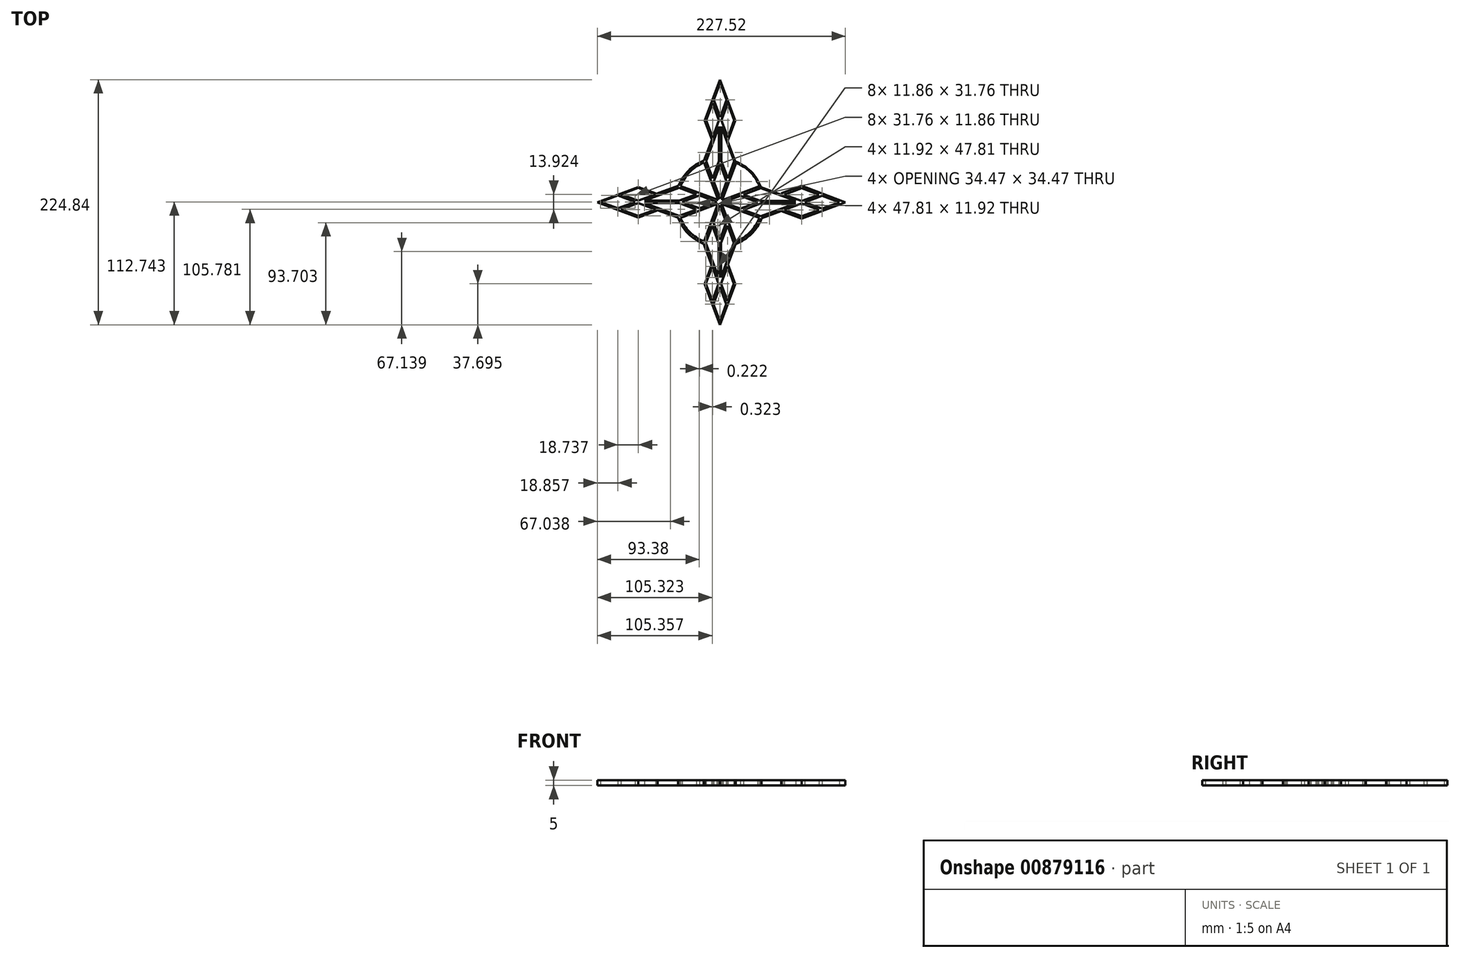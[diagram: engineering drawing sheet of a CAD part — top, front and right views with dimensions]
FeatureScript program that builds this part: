
annotation { "Feature Type Name" : "Feature", "Feature Type Description" : "" }
export const myFeature = defineFeature(function(context is Context, id is Id, definition is map)
    precondition{}
    {
        {
            var Q0;
            Q0=qCreatedBy(makeId("Top.planeOp"),FACE);
            var sketch = newSketch(context, id + "F0", { "sketchPlane" : qUnion([Q0])});
            skLineSegment(sketch, "E0", {"start": v(0, 0) * mm, "end": v(-14, 37.47) * mm});
            skLineSegment(sketch, "E1", {"start": v(-14, 37.47) * mm, "end": v(0, 74.95) * mm});
            skLineSegment(sketch, "E2", {"start": v(0, 74.95) * mm, "end": v(14, 37.47) * mm});
            skLineSegment(sketch, "E3", {"start": v(14, 37.47) * mm, "end": v(0, 0) * mm});
            skLineSegment(sketch, "E4", {"start": v(0, 74.95) * mm, "end": v(0, 37.47) * mm});
            skLineSegment(sketch, "E5", {"start": v(0, 37.47) * mm, "end": v(-7, 18.74) * mm});
            skLineSegment(sketch, "E6", {"start": v(0, 37.47) * mm, "end": v(7, 18.74) * mm});
            skLineSegment(sketch, "E7", {"start": v(-7, 56.2) * mm, "end": v(-14, 74.95) * mm});
            skLineSegment(sketch, "E8", {"start": v(-14, 74.95) * mm, "end": v(0, 112.42) * mm});
            skLineSegment(sketch, "E9", {"start": v(0, 112.42) * mm, "end": v(14, 74.95) * mm});
            skLineSegment(sketch, "E10", {"start": v(14, 74.95) * mm, "end": v(7, 56.2) * mm});
            skLineSegment(sketch, "E11", {"start": v(-7, 93.68) * mm, "end": v(0, 74.95) * mm});
            skLineSegment(sketch, "E12", {"start": v(7, 93.68) * mm, "end": v(0, 74.95) * mm});
            skLineSegment(sketch, "E13.1.0", {"start": v(-37.47, -14) * mm, "end": v(-74.95, 0) * mm});
            skLineSegment(sketch, "E13.1.1", {"start": v(-74.95, 0) * mm, "end": v(-37.47, 14) * mm});
            skLineSegment(sketch, "E13.1.2", {"start": v(-37.47, 0) * mm, "end": v(-18.74, 7) * mm});
            skLineSegment(sketch, "E13.1.3", {"start": v(-74.95, 0) * mm, "end": v(-37.47, 0) * mm});
            skLineSegment(sketch, "E13.1.4", {"start": v(-93.68, 7) * mm, "end": v(-74.95, 0) * mm});
            skLineSegment(sketch, "E13.1.5", {"start": v(-56.2, -7) * mm, "end": v(-74.95, -14) * mm});
            skLineSegment(sketch, "E13.1.6", {"start": v(-74.95, -14) * mm, "end": v(-112.42, 0) * mm});
            skLineSegment(sketch, "E13.1.7", {"start": v(-112.42, 0) * mm, "end": v(-74.95, 14) * mm});
            skLineSegment(sketch, "E13.1.8", {"start": v(-37.47, 0) * mm, "end": v(-18.74, -7) * mm});
            skLineSegment(sketch, "E13.1.9", {"start": v(-93.68, -7) * mm, "end": v(-74.95, 0) * mm});
            skLineSegment(sketch, "E13.1.10", {"start": v(-74.95, 14) * mm, "end": v(-56.2, 7) * mm});
            skLineSegment(sketch, "E13.1.11", {"start": v(0, 0) * mm, "end": v(-37.47, -14) * mm});
            skLineSegment(sketch, "E13.1.12", {"start": v(-37.47, 14) * mm, "end": v(0, 0) * mm});
            skLineSegment(sketch, "E13.2.0", {"start": v(14, -37.47) * mm, "end": v(0, -74.95) * mm});
            skLineSegment(sketch, "E13.2.1", {"start": v(0, -74.95) * mm, "end": v(-14, -37.47) * mm});
            skLineSegment(sketch, "E13.2.2", {"start": v(0, -37.47) * mm, "end": v(-7, -18.74) * mm});
            skLineSegment(sketch, "E13.2.3", {"start": v(0, -74.95) * mm, "end": v(0, -37.47) * mm});
            skLineSegment(sketch, "E13.2.4", {"start": v(-7, -93.68) * mm, "end": v(0, -74.95) * mm});
            skLineSegment(sketch, "E13.2.5", {"start": v(7, -56.2) * mm, "end": v(14, -74.95) * mm});
            skLineSegment(sketch, "E13.2.6", {"start": v(14, -74.95) * mm, "end": v(0, -112.42) * mm});
            skLineSegment(sketch, "E13.2.7", {"start": v(0, -112.42) * mm, "end": v(-14, -74.95) * mm});
            skLineSegment(sketch, "E13.2.8", {"start": v(0, -37.47) * mm, "end": v(7, -18.74) * mm});
            skLineSegment(sketch, "E13.2.9", {"start": v(7, -93.68) * mm, "end": v(0, -74.95) * mm});
            skLineSegment(sketch, "E13.2.10", {"start": v(-14, -74.95) * mm, "end": v(-7, -56.2) * mm});
            skLineSegment(sketch, "E13.2.11", {"start": v(0, 0) * mm, "end": v(14, -37.47) * mm});
            skLineSegment(sketch, "E13.2.12", {"start": v(-14, -37.47) * mm, "end": v(0, 0) * mm});
            skLineSegment(sketch, "E13.3.0", {"start": v(37.47, 14) * mm, "end": v(74.95, 0) * mm});
            skLineSegment(sketch, "E13.3.1", {"start": v(74.95, 0) * mm, "end": v(37.47, -14) * mm});
            skLineSegment(sketch, "E13.3.2", {"start": v(37.47, 0) * mm, "end": v(18.74, -7) * mm});
            skLineSegment(sketch, "E13.3.3", {"start": v(74.95, 0) * mm, "end": v(37.47, 0) * mm});
            skLineSegment(sketch, "E13.3.4", {"start": v(93.68, -7) * mm, "end": v(74.95, 0) * mm});
            skLineSegment(sketch, "E13.3.5", {"start": v(56.2, 7) * mm, "end": v(74.95, 14) * mm});
            skLineSegment(sketch, "E13.3.6", {"start": v(74.95, 14) * mm, "end": v(112.42, 0) * mm});
            skLineSegment(sketch, "E13.3.7", {"start": v(112.42, 0) * mm, "end": v(74.95, -14) * mm});
            skLineSegment(sketch, "E13.3.8", {"start": v(37.47, 0) * mm, "end": v(18.74, 7) * mm});
            skLineSegment(sketch, "E13.3.9", {"start": v(93.68, 7) * mm, "end": v(74.95, 0) * mm});
            skLineSegment(sketch, "E13.3.10", {"start": v(74.95, -14) * mm, "end": v(56.2, -7) * mm});
            skLineSegment(sketch, "E13.3.11", {"start": v(0, 0) * mm, "end": v(37.47, 14) * mm});
            skLineSegment(sketch, "E13.3.12", {"start": v(37.47, -14) * mm, "end": v(0, 0) * mm});
            skPoint(sketch, "E13.center", {"position": v(0, 0) * mm});
            skArc(sketch, "E14", {"start": v(14, 37.47) * mm, "mid": v(28.28, 28.28) * mm, "end": v(37.47, 14) * mm});
            skArc(sketch, "E15.1.0", {"start": v(-37.47, 14) * mm, "mid": v(-28.28, 28.28) * mm, "end": v(-14, 37.47) * mm});
            skArc(sketch, "E15.2.0", {"start": v(-14, -37.47) * mm, "mid": v(-28.28, -28.28) * mm, "end": v(-37.47, -14) * mm});
            skArc(sketch, "E16.3.3.0", {"start": v(37.47, -14) * mm, "mid": v(28.28, -28.28) * mm, "end": v(14, -37.47) * mm});
            skLineSegment(sketch, "E17", {"start": v(0, 0) * mm, "end": v(18.74, 7) * mm});
            skLineSegment(sketch, "E18", {"start": v(2.86, 0) * mm, "end": v(18.74, 5.93) * mm});
            skLineSegment(sketch, "E19", {"start": v(18.74, 5.93) * mm, "end": v(34.61, 0) * mm});
            skLineSegment(sketch, "E20", {"start": v(34.61, 0) * mm, "end": v(18.74, -5.93) * mm});
            skLineSegment(sketch, "E21", {"start": v(18.74, -5.93) * mm, "end": v(2.86, 0) * mm});
            skLineSegment(sketch, "E22", {"start": v(21.6, 7) * mm, "end": v(37.47, 12.92) * mm});
            skLineSegment(sketch, "E23", {"start": v(37.47, 12.92) * mm, "end": v(69.4, 1) * mm});
            skLineSegment(sketch, "E24", {"start": v(69.4, 1) * mm, "end": v(37.47, 1) * mm});
            skLineSegment(sketch, "E25", {"start": v(37.47, 1) * mm, "end": v(21.6, 7) * mm});
            skLineSegment(sketch, "E26", {"start": v(59.07, 7) * mm, "end": v(74.95, 12.92) * mm});
            skLineSegment(sketch, "E27", {"start": v(74.95, 12.92) * mm, "end": v(90.82, 7) * mm});
            skLineSegment(sketch, "E28", {"start": v(90.82, 7) * mm, "end": v(74.95, 1.07) * mm});
            skLineSegment(sketch, "E29", {"start": v(74.95, 1.07) * mm, "end": v(59.07, 7) * mm});
            skLineSegment(sketch, "E30", {"start": v(77.8, 0) * mm, "end": v(93.68, 5.93) * mm});
            skLineSegment(sketch, "E31", {"start": v(93.68, 5.93) * mm, "end": v(109.56, 0) * mm});
            skLineSegment(sketch, "E32", {"start": v(109.56, 0) * mm, "end": v(93.68, -5.93) * mm});
            skLineSegment(sketch, "E33", {"start": v(93.68, -5.93) * mm, "end": v(77.8, 0) * mm});
            skLineSegment(sketch, "E34", {"start": v(59.07, -7) * mm, "end": v(74.95, -1.07) * mm});
            skLineSegment(sketch, "E35", {"start": v(74.95, -1.07) * mm, "end": v(90.82, -7) * mm});
            skLineSegment(sketch, "E36", {"start": v(90.82, -7) * mm, "end": v(74.95, -12.92) * mm});
            skLineSegment(sketch, "E37", {"start": v(74.95, -12.92) * mm, "end": v(59.07, -7) * mm});
            skLineSegment(sketch, "E38.0", {"start": v(1.7, -1.7) * mm, "end": v(14.57, -36.17) * mm});
            skLineSegment(sketch, "E38.1", {"start": v(36.17, -14.57) * mm, "end": v(1.7, -1.7) * mm});
            skArc(sketch, "E38.2", {"start": v(36.17, -14.57) * mm, "mid": v(27.58, -27.58) * mm, "end": v(14.57, -36.17) * mm});
            skLineSegment(sketch, "E39.MirrorCS", {"start": v(69.4, -1) * mm, "end": v(37.47, -1) * mm});
            skLineSegment(sketch, "E40.MirrorCS", {"start": v(37.47, -1) * mm, "end": v(21.6, -7) * mm});
            skLineSegment(sketch, "E41.MirrorCS", {"start": v(21.6, -7) * mm, "end": v(37.47, -12.92) * mm});
            skLineSegment(sketch, "E42.MirrorCS", {"start": v(37.47, -12.92) * mm, "end": v(69.4, -1) * mm});
            skLineSegment(sketch, "E43.1.0", {"start": v(-6.77, 21.7) * mm, "end": v(-12.7, 37.57) * mm});
            skLineSegment(sketch, "E43.1.1", {"start": v(-12.7, 37.57) * mm, "end": v(-0.78, 69.51) * mm});
            skLineSegment(sketch, "E43.1.2", {"start": v(-0.78, 37.57) * mm, "end": v(-6.77, 21.7) * mm});
            skLineSegment(sketch, "E43.1.3", {"start": v(-0.78, 69.51) * mm, "end": v(-0.78, 37.57) * mm});
            skLineSegment(sketch, "E43.1.4", {"start": v(-5.7, 18.84) * mm, "end": v(0.22, 34.72) * mm});
            skLineSegment(sketch, "E43.1.5", {"start": v(0.22, 2.96) * mm, "end": v(-5.7, 18.84) * mm});
            skLineSegment(sketch, "E43.1.6", {"start": v(6.15, 18.84) * mm, "end": v(0.22, 2.96) * mm});
            skLineSegment(sketch, "E43.1.7", {"start": v(0.22, 34.72) * mm, "end": v(6.15, 18.84) * mm});
            skLineSegment(sketch, "E43.1.8", {"start": v(14.8, 36.28) * mm, "end": v(1.93, 1.8) * mm});
            skLineSegment(sketch, "E43.1.9", {"start": v(1.93, 1.8) * mm, "end": v(36.4, 14.67) * mm});
            skArc(sketch, "E43.1.10", {"start": v(14.8, 36.28) * mm, "mid": v(27.8, 27.68) * mm, "end": v(36.4, 14.67) * mm});
            skLineSegment(sketch, "E43.1.11", {"start": v(1.22, 37.57) * mm, "end": v(7.22, 21.7) * mm});
            skLineSegment(sketch, "E43.1.12", {"start": v(7.22, 21.7) * mm, "end": v(13.15, 37.57) * mm});
            skLineSegment(sketch, "E43.1.13", {"start": v(1.22, 69.51) * mm, "end": v(1.22, 37.57) * mm});
            skLineSegment(sketch, "E43.1.14", {"start": v(13.15, 37.57) * mm, "end": v(1.22, 69.51) * mm});
            skLineSegment(sketch, "E43.1.15", {"start": v(13.15, 75.05) * mm, "end": v(7.22, 59.17) * mm});
            skLineSegment(sketch, "E43.1.16", {"start": v(7.22, 59.17) * mm, "end": v(1.29, 75.05) * mm});
            skLineSegment(sketch, "E43.1.17", {"start": v(1.29, 75.05) * mm, "end": v(7.22, 90.93) * mm});
            skLineSegment(sketch, "E43.1.18", {"start": v(7.22, 90.93) * mm, "end": v(13.15, 75.05) * mm});
            skLineSegment(sketch, "E43.1.19", {"start": v(6.15, 93.78) * mm, "end": v(0.22, 77.9) * mm});
            skLineSegment(sketch, "E43.1.20", {"start": v(0.22, 77.9) * mm, "end": v(-5.7, 93.78) * mm});
            skLineSegment(sketch, "E43.1.21", {"start": v(-5.7, 93.78) * mm, "end": v(0.22, 109.66) * mm});
            skLineSegment(sketch, "E43.1.22", {"start": v(0.22, 109.66) * mm, "end": v(6.15, 93.78) * mm});
            skLineSegment(sketch, "E43.1.23", {"start": v(-6.77, 90.93) * mm, "end": v(-0.85, 75.05) * mm});
            skLineSegment(sketch, "E43.1.24", {"start": v(-12.7, 75.05) * mm, "end": v(-6.77, 90.93) * mm});
            skLineSegment(sketch, "E43.1.25", {"start": v(-6.77, 59.17) * mm, "end": v(-12.7, 75.05) * mm});
            skLineSegment(sketch, "E43.1.26", {"start": v(-0.85, 75.05) * mm, "end": v(-6.77, 59.17) * mm});
            skLineSegment(sketch, "E43.2.0", {"start": v(-21.48, -6.67) * mm, "end": v(-37.35, -12.6) * mm});
            skLineSegment(sketch, "E43.2.1", {"start": v(-37.35, -12.6) * mm, "end": v(-69.29, -0.68) * mm});
            skLineSegment(sketch, "E43.2.2", {"start": v(-37.35, -0.68) * mm, "end": v(-21.48, -6.67) * mm});
            skLineSegment(sketch, "E43.2.3", {"start": v(-69.29, -0.68) * mm, "end": v(-37.35, -0.68) * mm});
            skLineSegment(sketch, "E43.2.4", {"start": v(-18.62, -5.6) * mm, "end": v(-34.5, 0.32) * mm});
            skLineSegment(sketch, "E43.2.5", {"start": v(-2.74, 0.32) * mm, "end": v(-18.62, -5.6) * mm});
            skLineSegment(sketch, "E43.2.6", {"start": v(-18.62, 6.25) * mm, "end": v(-2.74, 0.32) * mm});
            skLineSegment(sketch, "E43.2.7", {"start": v(-34.5, 0.32) * mm, "end": v(-18.62, 6.25) * mm});
            skLineSegment(sketch, "E43.2.8", {"start": v(-36.05, 14.9) * mm, "end": v(-1.58, 2.03) * mm});
            skLineSegment(sketch, "E43.2.9", {"start": v(-1.58, 2.03) * mm, "end": v(-14.45, 36.5) * mm});
            skArc(sketch, "E43.2.10", {"start": v(-36.05, 14.9) * mm, "mid": v(-27.46, 27.9) * mm, "end": v(-14.45, 36.5) * mm});
            skLineSegment(sketch, "E43.2.11", {"start": v(-37.35, 1.32) * mm, "end": v(-21.48, 7.32) * mm});
            skLineSegment(sketch, "E43.2.12", {"start": v(-21.48, 7.32) * mm, "end": v(-37.35, 13.25) * mm});
            skLineSegment(sketch, "E43.2.13", {"start": v(-69.29, 1.32) * mm, "end": v(-37.35, 1.32) * mm});
            skLineSegment(sketch, "E43.2.14", {"start": v(-37.35, 13.25) * mm, "end": v(-69.29, 1.32) * mm});
            skLineSegment(sketch, "E43.2.15", {"start": v(-74.83, 13.25) * mm, "end": v(-58.95, 7.32) * mm});
            skLineSegment(sketch, "E43.2.16", {"start": v(-58.95, 7.32) * mm, "end": v(-74.83, 1.4) * mm});
            skLineSegment(sketch, "E43.2.17", {"start": v(-74.83, 1.4) * mm, "end": v(-90.7, 7.32) * mm});
            skLineSegment(sketch, "E43.2.18", {"start": v(-90.7, 7.32) * mm, "end": v(-74.83, 13.25) * mm});
            skLineSegment(sketch, "E43.2.19", {"start": v(-93.56, 6.25) * mm, "end": v(-77.68, 0.32) * mm});
            skLineSegment(sketch, "E43.2.20", {"start": v(-77.68, 0.32) * mm, "end": v(-93.56, -5.6) * mm});
            skLineSegment(sketch, "E43.2.21", {"start": v(-93.56, -5.6) * mm, "end": v(-109.44, 0.32) * mm});
            skLineSegment(sketch, "E43.2.22", {"start": v(-109.44, 0.32) * mm, "end": v(-93.56, 6.25) * mm});
            skLineSegment(sketch, "E43.2.23", {"start": v(-90.7, -6.67) * mm, "end": v(-74.83, -0.74) * mm});
            skLineSegment(sketch, "E43.2.24", {"start": v(-74.83, -12.6) * mm, "end": v(-90.7, -6.67) * mm});
            skLineSegment(sketch, "E43.2.25", {"start": v(-58.95, -6.67) * mm, "end": v(-74.83, -12.6) * mm});
            skLineSegment(sketch, "E43.2.26", {"start": v(-74.83, -0.74) * mm, "end": v(-58.95, -6.67) * mm});
            skLineSegment(sketch, "E43.3.0", {"start": v(6.9, -21.37) * mm, "end": v(12.82, -37.25) * mm});
            skLineSegment(sketch, "E43.3.1", {"start": v(12.82, -37.25) * mm, "end": v(0.9, -69.19) * mm});
            skLineSegment(sketch, "E43.3.2", {"start": v(0.9, -37.25) * mm, "end": v(6.9, -21.37) * mm});
            skLineSegment(sketch, "E43.3.3", {"start": v(0.9, -69.19) * mm, "end": v(0.9, -37.25) * mm});
            skLineSegment(sketch, "E43.3.4", {"start": v(5.83, -18.51) * mm, "end": v(-0.1, -34.4) * mm});
            skLineSegment(sketch, "E43.3.5", {"start": v(-0.1, -2.64) * mm, "end": v(5.83, -18.51) * mm});
            skLineSegment(sketch, "E43.3.6", {"start": v(-6.03, -18.51) * mm, "end": v(-0.1, -2.64) * mm});
            skLineSegment(sketch, "E43.3.7", {"start": v(-0.1, -34.4) * mm, "end": v(-6.03, -18.51) * mm});
            skLineSegment(sketch, "E43.3.8", {"start": v(-14.67, -35.95) * mm, "end": v(-1.8, -1.48) * mm});
            skLineSegment(sketch, "E43.3.9", {"start": v(-1.8, -1.48) * mm, "end": v(-36.28, -14.35) * mm});
            skArc(sketch, "E43.3.10", {"start": v(-14.67, -35.95) * mm, "mid": v(-27.68, -27.36) * mm, "end": v(-36.28, -14.35) * mm});
            skLineSegment(sketch, "E43.3.11", {"start": v(-1.1, -37.25) * mm, "end": v(-7.1, -21.37) * mm});
            skLineSegment(sketch, "E43.3.12", {"start": v(-7.1, -21.37) * mm, "end": v(-13.02, -37.25) * mm});
            skLineSegment(sketch, "E43.3.13", {"start": v(-1.1, -69.19) * mm, "end": v(-1.1, -37.25) * mm});
            skLineSegment(sketch, "E43.3.14", {"start": v(-13.02, -37.25) * mm, "end": v(-1.1, -69.19) * mm});
            skLineSegment(sketch, "E43.3.15", {"start": v(-13.02, -74.72) * mm, "end": v(-7.1, -58.85) * mm});
            skLineSegment(sketch, "E43.3.16", {"start": v(-7.1, -58.85) * mm, "end": v(-1.17, -74.72) * mm});
            skLineSegment(sketch, "E43.3.17", {"start": v(-1.17, -74.72) * mm, "end": v(-7.1, -90.6) * mm});
            skLineSegment(sketch, "E43.3.18", {"start": v(-7.1, -90.6) * mm, "end": v(-13.02, -74.72) * mm});
            skLineSegment(sketch, "E43.3.19", {"start": v(-6.03, -93.46) * mm, "end": v(-0.1, -77.58) * mm});
            skLineSegment(sketch, "E43.3.20", {"start": v(-0.1, -77.58) * mm, "end": v(5.83, -93.46) * mm});
            skLineSegment(sketch, "E43.3.21", {"start": v(5.83, -93.46) * mm, "end": v(-0.1, -109.34) * mm});
            skLineSegment(sketch, "E43.3.22", {"start": v(-0.1, -109.34) * mm, "end": v(-6.03, -93.46) * mm});
            skLineSegment(sketch, "E43.3.23", {"start": v(6.9, -90.6) * mm, "end": v(0.97, -74.72) * mm});
            skLineSegment(sketch, "E43.3.24", {"start": v(12.82, -74.72) * mm, "end": v(6.9, -90.6) * mm});
            skLineSegment(sketch, "E43.3.25", {"start": v(6.9, -58.85) * mm, "end": v(12.82, -74.72) * mm});
            skLineSegment(sketch, "E43.3.26", {"start": v(0.97, -74.72) * mm, "end": v(6.9, -58.85) * mm});
            skPoint(sketch, "E43.center", {"position": v(0.06, 0.16) * mm});
            skArc(sketch, "E44.0", {"start": v(38.25, -14.77) * mm, "mid": v(28.8, -29.18) * mm, "end": v(14.26, -38.44) * mm});
            skLineSegment(sketch, "E45", {"start": v(38.25, -14.77) * mm, "end": v(57.64, -7.53) * mm});
            skArc(sketch, "E46.1.0", {"start": v(14.8, 38.18) * mm, "mid": v(29.21, 28.73) * mm, "end": v(38.47, 14.19) * mm});
            skArc(sketch, "E46.2.0", {"start": v(-38.15, 14.72) * mm, "mid": v(-28.7, 29.14) * mm, "end": v(-14.16, 38.4) * mm});
            skArc(sketch, "E46.3.0", {"start": v(-14.7, -38.22) * mm, "mid": v(-29.11, -28.77) * mm, "end": v(-38.37, -14.23) * mm});
            skPoint(sketch, "E46.center", {"position": v(0.05, -0.02) * mm});
            skLineSegment(sketch, "E47", {"start": v(14.26, -38.44) * mm, "end": v(7.31, -57.05) * mm});
            skLineSegment(sketch, "E48", {"start": v(74.95, 15) * mm, "end": v(56.3, 8.03) * mm});
            skLineSegment(sketch, "E49", {"start": v(74.95, -15) * mm, "end": v(56.3, -8.03) * mm});
            skLineSegment(sketch, "E50", {"start": v(74.95, 15) * mm, "end": v(115.1, 0) * mm});
            skLineSegment(sketch, "E51", {"start": v(115.1, 0) * mm, "end": v(74.95, -15) * mm});
            skLineSegment(sketch, "E52", {"start": v(-56.98, -7.28) * mm, "end": v(-37.22, -14.66) * mm});
            skLineSegment(sketch, "E53", {"start": v(-7.1, -58.85) * mm, "end": v(-7.54, -57.66) * mm});
            skLineSegment(sketch, "E54", {"start": v(-7.54, -57.66) * mm, "end": v(-14.82, -38.17) * mm});
            skLineSegment(sketch, "E55", {"start": v(-58.01, 7.67) * mm, "end": v(-37.98, 15.15) * mm});
            skLineSegment(sketch, "E56", {"start": v(7.53, 57.64) * mm, "end": v(14.8, 38.18) * mm});
            skLineSegment(sketch, "E57", {"start": v(59.07, 7) * mm, "end": v(56.3, 8.03) * mm});
            skLineSegment(sketch, "E58", {"start": v(56.3, 8.03) * mm, "end": v(38.25, 14.77) * mm});
            skLineSegment(sketch, "E59", {"start": v(-6.77, 59.17) * mm, "end": v(-7.44, 57.4) * mm});
            skLineSegment(sketch, "E60", {"start": v(-7.44, 57.4) * mm, "end": v(-15.38, 36.1) * mm});
            skSolve(sketch);
        }
        {
            var Q0;
            {var subQ6=sQuery(id+"F0.wireOp",EDGE,"E11");Q0=makeQuery(id+"F0.imprint","IMPRINT",FACE,{"disambiguationData":[TD([[makeQuery(id+"F0.imprint","IMPRINT",EDGE,{"derivedFrom":subQ6}),-1.0]])]});}
            var Q1;
            {var subQ4=sQuery(id+"F0.wireOp",EDGE,"E11");Q1=makeQuery(id+"F0.imprint","IMPRINT",FACE,{"disambiguationData":[TD([[makeQuery(id+"F0.imprint","IMPRINT",EDGE,{"derivedFrom":subQ4}),1.0]])]});}
            var Q2;
            {var subQ6=sQuery(id+"F0.wireOp",EDGE,"E12");Q2=makeQuery(id+"F0.imprint","IMPRINT",FACE,{"disambiguationData":[TD([[makeQuery(id+"F0.imprint","IMPRINT",EDGE,{"derivedFrom":subQ6}),1.0]])]});}
            var Q3;
            {var subQ0=sQuery(id+"F0.wireOp",EDGE,"E4");Q3=makeQuery(id+"F0.imprint","IMPRINT",FACE,{"disambiguationData":[TD([[makeQuery(id+"F0.imprint","IMPRINT",EDGE,{"derivedFrom":subQ0}),1.0]])]});}
            var Q4;
            {var subQ0=sQuery(id+"F0.wireOp",EDGE,"E4");Q4=makeQuery(id+"F0.imprint","IMPRINT",FACE,{"disambiguationData":[TD([[makeQuery(id+"F0.imprint","IMPRINT",EDGE,{"derivedFrom":subQ0}),-1.0]])]});}
            var Q5;
            {var subQ0=sQuery(id+"F0.wireOp",EDGE,"E5");Q5=makeQuery(id+"F0.imprint","IMPRINT",FACE,{"disambiguationData":[TD([[makeQuery(id+"F0.imprint","IMPRINT",EDGE,{"derivedFrom":subQ0}),1.0]])]});}
            var Q6;
            Q6=makeQuery(id+"F0.imprint","IMPRINT",FACE,{"disambiguationData":[TD([[makeQuery(id+"F0.imprint","IMPRINT",EDGE,{"derivedFrom":sQuery(id+"F0.wireOp",EDGE,"E13.3.11")}),1.0]])]});
            var Q7;
            {var subQ0=sQuery(id+"F0.wireOp",EDGE,"E14");Q7=makeQuery(id+"F0.imprint","IMPRINT",FACE,{"disambiguationData":[TD([[makeQuery(id+"F0.imprint","IMPRINT",EDGE,{"derivedFrom":subQ0}),1.0]])]});}
            var Q8;
            {var subQ0=sQuery(id+"F0.wireOp",EDGE,"E15.1.0");Q8=makeQuery(id+"F0.imprint","IMPRINT",FACE,{"disambiguationData":[TD([[makeQuery(id+"F0.imprint","IMPRINT",EDGE,{"derivedFrom":subQ0}),1.0]])]});}
            var Q9;
            {var subQ4=sQuery(id+"F0.wireOp",EDGE,"E15.1.0");Q9=makeQuery(id+"F0.imprint","IMPRINT",FACE,{"disambiguationData":[TD([[makeQuery(id+"F0.imprint","IMPRINT",EDGE,{"derivedFrom":subQ4}),-1.0]])]});}
            var Q10;
            {var subQ0=sQuery(id+"F0.wireOp",EDGE,"E13.3.3");Q10=makeQuery(id+"F0.imprint","IMPRINT",FACE,{"disambiguationData":[TD([[makeQuery(id+"F0.imprint","IMPRINT",EDGE,{"derivedFrom":subQ0}),-1.0]])]});}
            var Q11;
            {var subQ2=sQuery(id+"F0.wireOp",EDGE,"E13.3.2");Q11=makeQuery(id+"F0.imprint","IMPRINT",FACE,{"disambiguationData":[TD([[makeQuery(id+"F0.imprint","IMPRINT",EDGE,{"derivedFrom":subQ2}),-1.0]])]});}
            var Q12;
            {var subQ3=sQuery(id+"F0.wireOp",EDGE,"E13.3.9");Q12=makeQuery(id+"F0.imprint","IMPRINT",FACE,{"disambiguationData":[TD([[makeQuery(id+"F0.imprint","IMPRINT",EDGE,{"derivedFrom":subQ3}),-1.0]])]});}
            var Q13;
            {var subQ4=sQuery(id+"F0.wireOp",EDGE,"E13.3.4");Q13=makeQuery(id+"F0.imprint","IMPRINT",FACE,{"disambiguationData":[TD([[makeQuery(id+"F0.imprint","IMPRINT",EDGE,{"derivedFrom":subQ4}),-1.0]])]});}
            var Q14;
            {var subQ4=sQuery(id+"F0.wireOp",EDGE,"E13.3.4");Q14=makeQuery(id+"F0.imprint","IMPRINT",FACE,{"disambiguationData":[TD([[makeQuery(id+"F0.imprint","IMPRINT",EDGE,{"derivedFrom":subQ4}),1.0]])]});}
            var Q15;
            {var subQ1=sQuery(id+"F0.wireOp",EDGE,"E13.3.2");Q15=makeQuery(id+"F0.imprint","IMPRINT",FACE,{"disambiguationData":[TD([[makeQuery(id+"F0.imprint","IMPRINT",EDGE,{"derivedFrom":subQ1}),1.0]])]});}
            var Q16;
            {var subQ0=sQuery(id+"F0.wireOp",EDGE,"E16.3.3.0");Q16=makeQuery(id+"F0.imprint","IMPRINT",FACE,{"disambiguationData":[TD([[makeQuery(id+"F0.imprint","IMPRINT",EDGE,{"derivedFrom":subQ0}),1.0]])]});}
            var Q17;
            {var subQ4=sQuery(id+"F0.wireOp",EDGE,"E16.3.3.0");Q17=makeQuery(id+"F0.imprint","IMPRINT",FACE,{"disambiguationData":[TD([[makeQuery(id+"F0.imprint","IMPRINT",EDGE,{"derivedFrom":subQ4}),-1.0]])]});}
            var Q18;
            {var subQ3=sQuery(id+"F0.wireOp",EDGE,"E13.1.2");Q18=makeQuery(id+"F0.imprint","IMPRINT",FACE,{"disambiguationData":[TD([[makeQuery(id+"F0.imprint","IMPRINT",EDGE,{"derivedFrom":subQ3}),-1.0]])]});}
            var Q19;
            {var subQ1=sQuery(id+"F0.wireOp",EDGE,"E13.1.2");Q19=makeQuery(id+"F0.imprint","IMPRINT",FACE,{"disambiguationData":[TD([[makeQuery(id+"F0.imprint","IMPRINT",EDGE,{"derivedFrom":subQ1}),1.0]])]});}
            var Q20;
            {var subQ1=sQuery(id+"F0.wireOp",EDGE,"E13.1.3");Q20=makeQuery(id+"F0.imprint","IMPRINT",FACE,{"disambiguationData":[TD([[makeQuery(id+"F0.imprint","IMPRINT",EDGE,{"derivedFrom":subQ1}),-1.0]])]});}
            var Q21;
            {var subQ4=sQuery(id+"F0.wireOp",EDGE,"E15.2.0");Q21=makeQuery(id+"F0.imprint","IMPRINT",FACE,{"disambiguationData":[TD([[makeQuery(id+"F0.imprint","IMPRINT",EDGE,{"derivedFrom":subQ4}),-1.0]])]});}
            var Q22;
            {var subQ3=sQuery(id+"F0.wireOp",EDGE,"E13.2.2");Q22=makeQuery(id+"F0.imprint","IMPRINT",FACE,{"disambiguationData":[TD([[makeQuery(id+"F0.imprint","IMPRINT",EDGE,{"derivedFrom":subQ3}),-1.0]])]});}
            var Q23;
            {var subQ3=sQuery(id+"F0.wireOp",EDGE,"E13.1.9");Q23=makeQuery(id+"F0.imprint","IMPRINT",FACE,{"disambiguationData":[TD([[makeQuery(id+"F0.imprint","IMPRINT",EDGE,{"derivedFrom":subQ3}),-1.0]])]});}
            var Q24;
            {var subQ4=sQuery(id+"F0.wireOp",EDGE,"E13.1.4");Q24=makeQuery(id+"F0.imprint","IMPRINT",FACE,{"disambiguationData":[TD([[makeQuery(id+"F0.imprint","IMPRINT",EDGE,{"derivedFrom":subQ4}),1.0]])]});}
            var Q25;
            {var subQ4=sQuery(id+"F0.wireOp",EDGE,"E13.1.4");Q25=makeQuery(id+"F0.imprint","IMPRINT",FACE,{"disambiguationData":[TD([[makeQuery(id+"F0.imprint","IMPRINT",EDGE,{"derivedFrom":subQ4}),-1.0]])]});}
            var Q26;
            {var subQ0=sQuery(id+"F0.wireOp",EDGE,"E15.2.0");Q26=makeQuery(id+"F0.imprint","IMPRINT",FACE,{"disambiguationData":[TD([[makeQuery(id+"F0.imprint","IMPRINT",EDGE,{"derivedFrom":subQ0}),1.0]])]});}
            var Q27;
            {var subQ1=sQuery(id+"F0.wireOp",EDGE,"E13.2.3");Q27=makeQuery(id+"F0.imprint","IMPRINT",FACE,{"disambiguationData":[TD([[makeQuery(id+"F0.imprint","IMPRINT",EDGE,{"derivedFrom":subQ1}),-1.0]])]});}
            var Q28;
            {var subQ1=sQuery(id+"F0.wireOp",EDGE,"E13.2.2");Q28=makeQuery(id+"F0.imprint","IMPRINT",FACE,{"disambiguationData":[TD([[makeQuery(id+"F0.imprint","IMPRINT",EDGE,{"derivedFrom":subQ1}),1.0]])]});}
            var Q29;
            {var subQ4=sQuery(id+"F0.wireOp",EDGE,"E13.2.4");Q29=makeQuery(id+"F0.imprint","IMPRINT",FACE,{"disambiguationData":[TD([[makeQuery(id+"F0.imprint","IMPRINT",EDGE,{"derivedFrom":subQ4}),1.0]])]});}
            var Q30;
            {var subQ3=sQuery(id+"F0.wireOp",EDGE,"E13.2.9");Q30=makeQuery(id+"F0.imprint","IMPRINT",FACE,{"disambiguationData":[TD([[makeQuery(id+"F0.imprint","IMPRINT",EDGE,{"derivedFrom":subQ3}),-1.0]])]});}
            var Q31;
            {var subQ4=sQuery(id+"F0.wireOp",EDGE,"E13.2.4");Q31=makeQuery(id+"F0.imprint","IMPRINT",FACE,{"disambiguationData":[TD([[makeQuery(id+"F0.imprint","IMPRINT",EDGE,{"derivedFrom":subQ4}),-1.0]])]});}
            var Q32;
            {var subQ4=sQuery(id+"F0.wireOp",EDGE,"E48");Q32=makeQuery(id+"F0.imprint","IMPRINT",FACE,{"disambiguationData":[TD([[makeQuery(id+"F0.imprint","IMPRINT",EDGE,{"derivedFrom":subQ4}),1.0]])]});}
            var Q33;
            {var subQ0=sQuery(id+"F0.wireOp",EDGE,"E55");Q33=makeQuery(id+"F0.imprint","IMPRINT",FACE,{"disambiguationData":[TD([[makeQuery(id+"F0.imprint","IMPRINT",EDGE,{"derivedFrom":subQ0}),-1.0]])]});}
            var Q34;
            {var subQ3=sQuery(id+"F0.wireOp",EDGE,"E54");Q34=makeQuery(id+"F0.imprint","IMPRINT",FACE,{"disambiguationData":[TD([[makeQuery(id+"F0.imprint","IMPRINT",EDGE,{"derivedFrom":subQ3}),-1.0]])]});}
            extrude(context, id + "F1", {"entities" : qUnion([Q0, Q1, Q2, Q3, Q4, Q5, Q6, Q7, Q8, Q9, Q10, Q11, Q12, Q13, Q14, Q15, Q16, Q17, Q18, Q19, Q20, Q21, Q22, Q23, Q24, Q25, Q26, Q27, Q28, Q29, Q30, Q31, Q32, Q33, Q34]), "depth" : 5 * mm, "offsetDistance" : 25 * mm});
        }
    });
